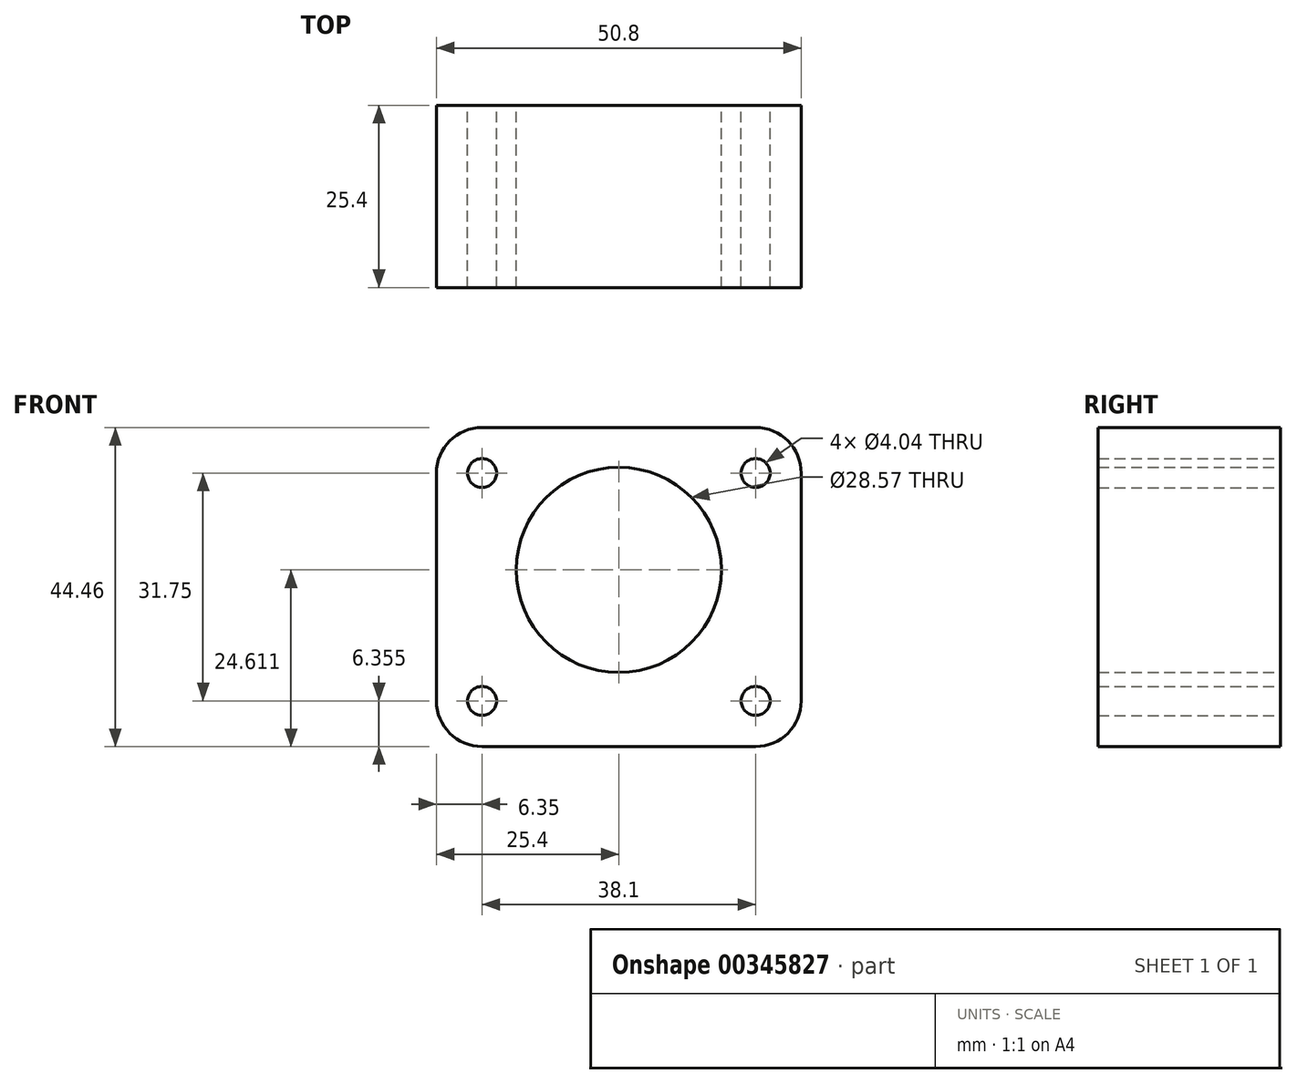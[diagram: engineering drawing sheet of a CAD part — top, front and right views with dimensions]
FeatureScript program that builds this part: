
annotation { "Feature Type Name" : "Feature", "Feature Type Description" : "" }
export const myFeature = defineFeature(function(context is Context, id is Id, definition is map)
    precondition{}
    {
        {
            var Q0;
            Q0=qCreatedBy(makeId("Front.planeOp"),FACE);
            var sketch = newSketch(context, id + "F0", { "sketchPlane" : qUnion([Q0])});
            skLineSegment(sketch, "E0.bottom", {"start": v(-25.4, 22.22) * mm, "end": v(25.4, 22.22) * mm});
            skLineSegment(sketch, "E0.top", {"start": v(-25.4, -22.23) * mm, "end": v(25.4, -22.23) * mm});
            skLineSegment(sketch, "E0.left", {"start": v(-25.4, 22.22) * mm, "end": v(-25.4, -22.23) * mm});
            skLineSegment(sketch, "E0.right", {"start": v(25.4, 22.22) * mm, "end": v(25.4, -22.23) * mm});
            skPoint(sketch, "E0.middle", {"position": v(0, 0) * mm});
            skLineSegment(sketch, "E1.bottom", {"start": v(-19.05, 15.88) * mm, "end": v(19.05, 15.88) * mm, "construction": true});
            skLineSegment(sketch, "E1.top", {"start": v(-19.05, -15.88) * mm, "end": v(19.05, -15.88) * mm, "construction": true});
            skLineSegment(sketch, "E1.left", {"start": v(-19.05, 15.88) * mm, "end": v(-19.05, -15.88) * mm, "construction": true});
            skLineSegment(sketch, "E1.right", {"start": v(19.05, 15.88) * mm, "end": v(19.05, -15.88) * mm, "construction": true});
            skCircle(sketch, "E2", {"center": v(-19.05, 15.88) * mm, "radius": 2.02 * mm});
            skCircle(sketch, "E3", {"center": v(19.05, 15.88) * mm, "radius": 2.02 * mm});
            skCircle(sketch, "E4", {"center": v(-19.05, -15.88) * mm, "radius": 2.02 * mm});
            skCircle(sketch, "E5", {"center": v(19.05, -15.88) * mm, "radius": 2.02 * mm});
            skCircle(sketch, "E6", {"center": v(0, 2.38) * mm, "radius": 14.29 * mm});
            skLineSegment(sketch, "E7", {"start": v(0, 2.38) * mm, "end": v(0, 0) * mm, "construction": true});
            skSolve(sketch);
        }
        {
            var Q0;
            Q0 = qSketchRegion(id + "F0", true);
            extrude(context, id + "F1", {"entities" : qUnion([Q0]), "endBound" : BoundingType.SYMMETRIC, "depth" : 25.4 * mm});
        }
        {
            var Q0;
            Q0=makeQuery(id+"F1.opExtrude","SWEPT_EDGE",EDGE,{"disambiguationData":[OSD([sQuery(id+"F0.wireOp",EDGE,"E0.top"),sQuery(id+"F0.wireOp",EDGE,"E0.right")])]});
            var Q1;
            Q1=makeQuery(id+"F1.opExtrude","SWEPT_EDGE",EDGE,{"disambiguationData":[OSD([sQuery(id+"F0.wireOp",EDGE,"E0.bottom"),sQuery(id+"F0.wireOp",EDGE,"E0.right")])]});
            var Q2;
            Q2=makeQuery(id+"F1.opExtrude","SWEPT_EDGE",EDGE,{"disambiguationData":[OSD([sQuery(id+"F0.wireOp",EDGE,"E0.bottom"),sQuery(id+"F0.wireOp",EDGE,"E0.left")])]});
            var Q3;
            Q3=makeQuery(id+"F1.opExtrude","SWEPT_EDGE",EDGE,{"disambiguationData":[OSD([sQuery(id+"F0.wireOp",EDGE,"E0.top"),sQuery(id+"F0.wireOp",EDGE,"E0.left")])]});
            fillet(context, id + "F2", {"entities" : qUnion([Q0, Q1, Q2, Q3]), "radius" : 6.35 * mm, "tangentPropagation" : true, "allowEdgeOverflow" : false});
        }
    });
